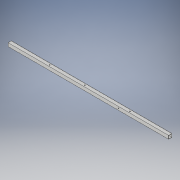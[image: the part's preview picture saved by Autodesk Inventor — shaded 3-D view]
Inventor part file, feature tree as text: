
AUTODESK INVENTOR PART (.ipt)
format: ipt  version: 2017 (Build 210142000, 142)  size: 124,928 bytes
history: native  units: in
note: dims shown in document units (in); Inventor stores cm internally (conversion verified against a paired STEP export)
features: extrude x3, sketch x3
ambient origin geometry x8: Origin, YZ Plane, XZ Plane, XY Plane, X Axis, Y Axis, Z Axis, Center Point
bodies: Solid1 (feature_tree)
feature tree (6):
  extrude  "Extrusion1"  Depth=1.0in
  extrude  "Extrusion3"  Depth=48.0in TaperAngle=0.0deg
  extrude  "Extrusion4"  Depth=1.0in
  sketch  "Sketch1"  dims[d0=1.0in d1=1.0in]
  sketch  "Sketch3"  dims[d2=0.0625in d3=48.0in d4=0.0in]
  sketch  "Sketch4"  dims[d10=0.25in d11=12.0in d12=1.0in d13=0.0in d14=1.5in d15=0.25in d17=1.0in d18=0.0in d19=9.0in]
